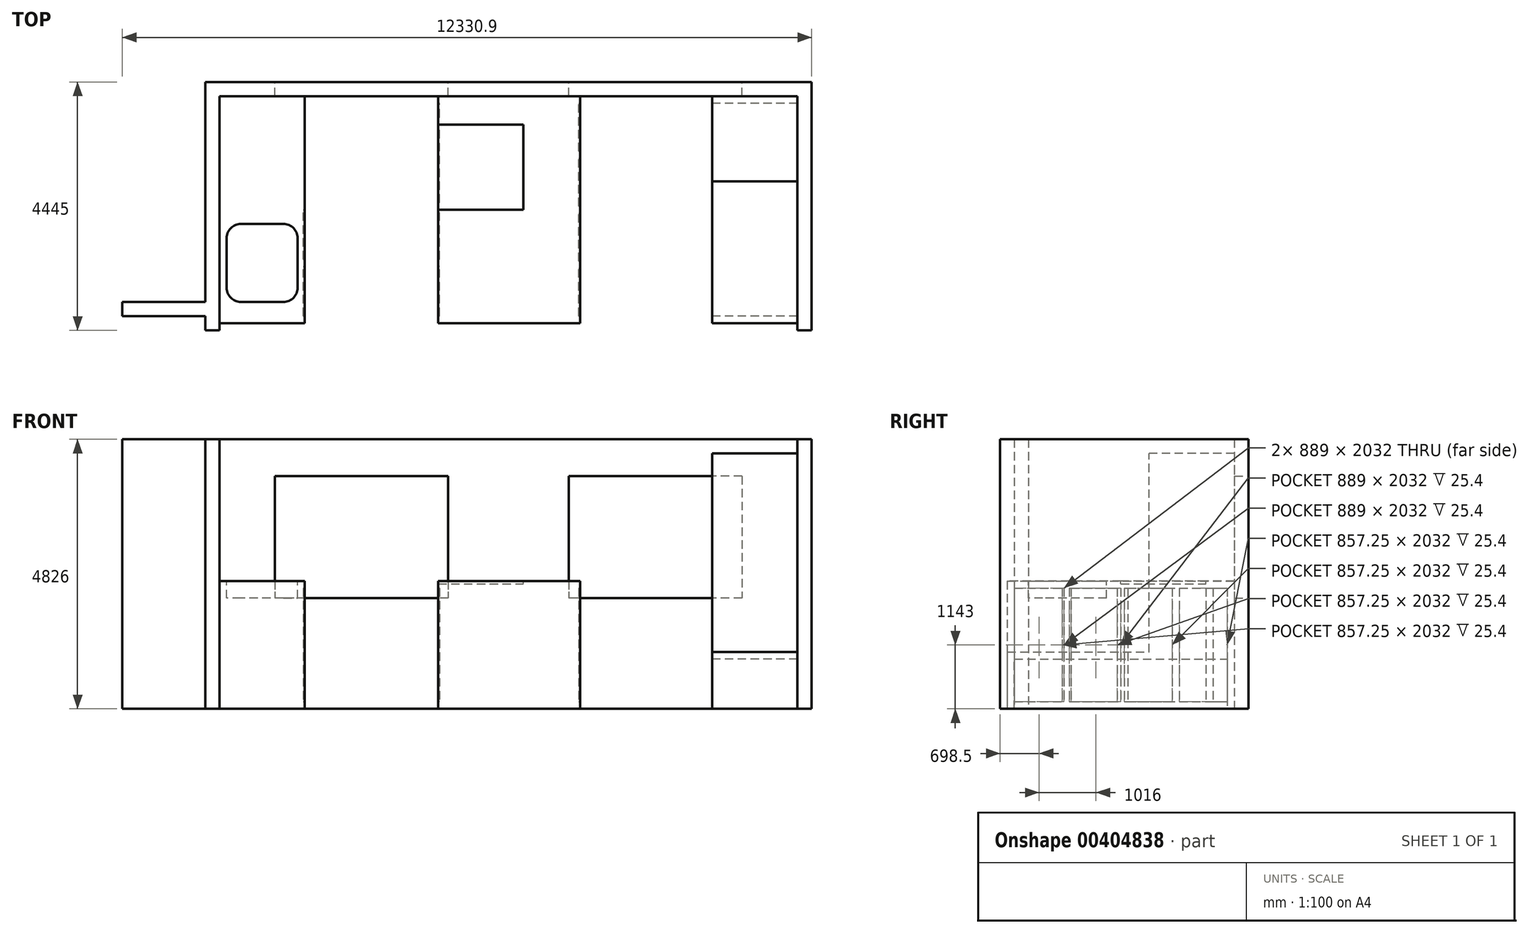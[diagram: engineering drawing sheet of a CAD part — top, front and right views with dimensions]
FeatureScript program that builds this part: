
annotation { "Feature Type Name" : "Feature", "Feature Type Description" : "" }
export const myFeature = defineFeature(function(context is Context, id is Id, definition is map)
    precondition{}
    {
        {
            var Q0;
            Q0=qCreatedBy(makeId("Top.planeOp"),FACE);
            var sketch = newSketch(context, id + "F0", { "sketchPlane" : qUnion([Q0])});
            skLineSegment(sketch, "E0", {"start": v(0, 0) * mm, "end": v(254, 0) * mm});
            skLineSegment(sketch, "E1", {"start": v(254, 0) * mm, "end": v(254, 4445) * mm});
            skLineSegment(sketch, "E2", {"start": v(254, 4445) * mm, "end": v(-10591.8, 4445) * mm});
            skLineSegment(sketch, "E3", {"start": v(-10591.8, 4445) * mm, "end": v(-10591.8, 508) * mm});
            skLineSegment(sketch, "E4", {"start": v(-10591.8, 508) * mm, "end": v(-12076.86, 508) * mm});
            skLineSegment(sketch, "E5", {"start": v(-12076.86, 508) * mm, "end": v(-12076.86, 254) * mm});
            skLineSegment(sketch, "E6", {"start": v(-12076.86, 254) * mm, "end": v(-10591.8, 254) * mm});
            skLineSegment(sketch, "E7", {"start": v(-10591.8, 254) * mm, "end": v(-10591.8, 0) * mm});
            skLineSegment(sketch, "E8", {"start": v(-10591.8, 0) * mm, "end": v(-10337.8, 0) * mm});
            skLineSegment(sketch, "E9", {"start": v(-10337.8, 0) * mm, "end": v(-10337.8, 4191) * mm});
            skLineSegment(sketch, "E10", {"start": v(-10337.8, 4191) * mm, "end": v(0, 4191) * mm});
            skLineSegment(sketch, "E11", {"start": v(0, 4191) * mm, "end": v(0, 0) * mm});
            skLineSegment(sketch, "E12", {"start": v(254, -2032) * mm, "end": v(0, -2032) * mm});
            skLineSegment(sketch, "E13", {"start": v(0, -2032) * mm, "end": v(0, -2286) * mm});
            skLineSegment(sketch, "E14", {"start": v(0, -2286) * mm, "end": v(-8051.8, -2286) * mm});
            skLineSegment(sketch, "E15", {"start": v(-10337.8, -2286) * mm, "end": v(-10337.8, -2032) * mm});
            skLineSegment(sketch, "E16", {"start": v(-10337.8, -2032) * mm, "end": v(-10591.8, -2032) * mm});
            skLineSegment(sketch, "E17", {"start": v(-10591.8, -2032) * mm, "end": v(-10591.8, -2286) * mm});
            skLineSegment(sketch, "E18", {"start": v(-10591.8, -2286) * mm, "end": v(-12107.08, -2286) * mm});
            skLineSegment(sketch, "E19", {"start": v(-12107.08, -2286) * mm, "end": v(-12107.08, -2540) * mm});
            skLineSegment(sketch, "E20", {"start": v(-12107.08, -2540) * mm, "end": v(-10591.8, -2540) * mm});
            skLineSegment(sketch, "E21", {"start": v(-10591.8, -2540) * mm, "end": v(-10591.8, -2794) * mm});
            skLineSegment(sketch, "E22", {"start": v(-10591.8, -2794) * mm, "end": v(-10337.8, -2794) * mm});
            skLineSegment(sketch, "E23", {"start": v(-10337.8, -2794) * mm, "end": v(-10337.8, -2540) * mm});
            skLineSegment(sketch, "E24", {"start": v(-10337.8, -2540) * mm, "end": v(-10083.8, -2540) * mm});
            skLineSegment(sketch, "E25", {"start": v(-10083.8, -2540) * mm, "end": v(-10083.8, -2286) * mm});
            skLineSegment(sketch, "E26", {"start": v(-8051.8, -2286) * mm, "end": v(-8051.8, -2540) * mm});
            skLineSegment(sketch, "E27", {"start": v(-8051.8, -2540) * mm, "end": v(0, -2540) * mm});
            skLineSegment(sketch, "E28", {"start": v(0, -2540) * mm, "end": v(0, -2794) * mm});
            skLineSegment(sketch, "E29", {"start": v(0, -2794) * mm, "end": v(254, -2794) * mm});
            skLineSegment(sketch, "E30", {"start": v(254, -2794) * mm, "end": v(254, -2540) * mm});
            skLineSegment(sketch, "E31", {"start": v(254, -2540) * mm, "end": v(508, -2540) * mm});
            skLineSegment(sketch, "E32", {"start": v(508, -2540) * mm, "end": v(508, -2286) * mm});
            skLineSegment(sketch, "E33", {"start": v(508, -2286) * mm, "end": v(254, -2286) * mm});
            skLineSegment(sketch, "E34", {"start": v(254, -2286) * mm, "end": v(254, -2032) * mm});
            skLineSegment(sketch, "E35.trimOffspring", {"start": v(-10083.8, -2286) * mm, "end": v(-10337.8, -2286) * mm});
            skLineSegment(sketch, "E36", {"start": v(-8813.8, 4191) * mm, "end": v(-8813.8, 127) * mm});
            skLineSegment(sketch, "E37", {"start": v(-8813.8, 127) * mm, "end": v(-10337.8, 127) * mm});
            skLineSegment(sketch, "E38", {"start": v(-6426.2, 4191) * mm, "end": v(-6426.2, 127) * mm});
            skLineSegment(sketch, "E39", {"start": v(-6426.2, 127) * mm, "end": v(-3886.2, 127) * mm});
            skLineSegment(sketch, "E40", {"start": v(-3886.2, 127) * mm, "end": v(-3886.2, 4191) * mm});
            skLineSegment(sketch, "E41", {"start": v(-6426.2, 3683) * mm, "end": v(-4902.2, 3683) * mm});
            skLineSegment(sketch, "E42", {"start": v(-4902.2, 3683) * mm, "end": v(-4902.2, 2159) * mm});
            skLineSegment(sketch, "E43", {"start": v(-4902.2, 2159) * mm, "end": v(-6426.2, 2159) * mm});
            skLineSegment(sketch, "E44", {"start": v(-1524, 4191) * mm, "end": v(-1524, 2667) * mm});
            skLineSegment(sketch, "E45", {"start": v(-1524, 2667) * mm, "end": v(0, 2667) * mm});
            skLineSegment(sketch, "E46", {"start": v(-1524, 2667) * mm, "end": v(-1524, 127) * mm});
            skLineSegment(sketch, "E47", {"start": v(-1524, 127) * mm, "end": v(0, 127) * mm});
            skLineSegment(sketch, "E48", {"start": v(-10337.8, 4191) * mm, "end": v(-8813.8, 4191) * mm});
            skLineSegment(sketch, "E49", {"start": v(-6426.2, 4191) * mm, "end": v(-3886.2, 4191) * mm});
            skLineSegment(sketch, "E50", {"start": v(-1524, 4191) * mm, "end": v(0, 4191) * mm});
            skSolve(sketch);
        }
        {
            var Q0;
            {var subQ0=sQuery(id+"F0.wireOp",EDGE,"E0");Q0=makeQuery(id+"F0.imprint","IMPRINT",FACE,{"disambiguationData":[TD([[makeQuery(id+"F0.imprint","IMPRINT",EDGE,{"derivedFrom":subQ0}),1.0]])]});}
            extrude(context, id + "F1", {"entities" : qUnion([Q0]), "depth" : 4826 * mm});
        }
        {
            var Q0;
            Q0=makeQuery(id+"F1.opExtrude","SWEPT_FACE",FACE,{"disambiguationData":[OSD([sQuery(id+"F0.wireOp",EDGE,"E2")])]});
            var sketch = newSketch(context, id + "F2", { "sketchPlane" : qUnion([Q0])});
            skLineSegment(sketch, "E51.bottom", {"start": v(990.6, 4165.6) * mm, "end": v(4089.4, 4165.6) * mm});
            skLineSegment(sketch, "E51.top", {"start": v(990.6, 1981.2) * mm, "end": v(4089.4, 1981.2) * mm});
            skLineSegment(sketch, "E51.left", {"start": v(990.6, 4165.6) * mm, "end": v(990.6, 1981.2) * mm});
            skLineSegment(sketch, "E51.right", {"start": v(4089.4, 4165.6) * mm, "end": v(4089.4, 1981.2) * mm});
            skLineSegment(sketch, "E52.bottom", {"start": v(6248.4, 4165.6) * mm, "end": v(9347.2, 4165.6) * mm});
            skLineSegment(sketch, "E52.top", {"start": v(6248.4, 1981.2) * mm, "end": v(9347.2, 1981.2) * mm});
            skLineSegment(sketch, "E52.left", {"start": v(6248.4, 4165.6) * mm, "end": v(6248.4, 1981.2) * mm});
            skLineSegment(sketch, "E52.right", {"start": v(9347.2, 4165.6) * mm, "end": v(9347.2, 1981.2) * mm});
            skSolve(sketch);
        }
        {
            var Q0;
            Q0=qSketchRegion(id+"F2",true);
            extrude(context, id + "F3", {"entities" : qUnion([Q0]), "operationType" : NewBodyOperationType.REMOVE, "oppositeDirection" : true, "depth" : 254 * mm});
        }
        {
            var Q0;
            Q0=makeQuery(id+"F0.imprint","IMPRINT",FACE,{"disambiguationData":[TD([[makeQuery(id+"F0.imprint","IMPRINT",EDGE,{"derivedFrom":sQuery(id+"F0.wireOp",EDGE,"E36")}),-1.0]])]});
            var Q1;
            {var subQ0=sQuery(id+"F0.wireOp",EDGE,"E41");Q1=makeQuery(id+"F0.imprint","IMPRINT",FACE,{"disambiguationData":[TD([[makeQuery(id+"F0.imprint","IMPRINT",EDGE,{"derivedFrom":subQ0}),-1.0]])]});}
            var Q2;
            {var subQ0=sQuery(id+"F0.wireOp",EDGE,"E39");Q2=makeQuery(id+"F0.imprint","IMPRINT",FACE,{"disambiguationData":[TD([[makeQuery(id+"F0.imprint","IMPRINT",EDGE,{"derivedFrom":subQ0}),1.0]])]});}
            extrude(context, id + "F4", {"entities" : qUnion([Q0, Q1, Q2]), "operationType" : NewBodyOperationType.ADD, "depth" : 2286 * mm});
        }
        {
            var Q0;
            {var subQ0=sQuery(id+"F0.wireOp",EDGE,"E45");Q0=makeQuery(id+"F0.imprint","IMPRINT",FACE,{"disambiguationData":[TD([[makeQuery(id+"F0.imprint","IMPRINT",EDGE,{"derivedFrom":subQ0}),-1.0]])]});}
            var Q1;
            {var subQ3=sQuery(id+"F0.wireOp",EDGE,"E44");Q1=makeQuery(id+"F0.imprint","IMPRINT",FACE,{"disambiguationData":[TD([[makeQuery(id+"F0.imprint","IMPRINT",EDGE,{"derivedFrom":subQ3}),1.0]])]});}
            extrude(context, id + "F5", {"entities" : qUnion([Q0, Q1]), "operationType" : NewBodyOperationType.ADD, "depth" : 4572 * mm});
        }
        {
            var Q0;
            Q0=makeQuery(id+"F5.opExtrude","SWEPT_FACE",FACE,{"disambiguationData":[OSD([sQuery(id+"F0.wireOp",EDGE,"E44"),sQuery(id+"F0.wireOp",EDGE,"E46")])]});
            var sketch = newSketch(context, id + "F6", { "sketchPlane" : qUnion([Q0])});
            skLineSegment(sketch, "E53", {"start": v(-254, 0) * mm, "end": v(-254, 889) * mm});
            skLineSegment(sketch, "E54", {"start": v(-254, 889) * mm, "end": v(-4064, 889) * mm});
            skLineSegment(sketch, "E55", {"start": v(-4064, 889) * mm, "end": v(-4064, 0) * mm});
            skLineSegment(sketch, "E56", {"start": v(-127, 1016) * mm, "end": v(-2667, 1016) * mm});
            skLineSegment(sketch, "E57", {"start": v(-2667, 1016) * mm, "end": v(-2667, 4572) * mm});
            skLineSegment(sketch, "E58", {"start": v(-2667, 1016) * mm, "end": v(-4191, 1016) * mm});
            skSolve(sketch);
        }
        {
            var Q0;
            Q0 = qSketchRegion(id + "F6", true);
            var Q1;
            {var subQ0=sQuery(id+"F6.wireOp",EDGE,"E56");Q1=makeQuery(id+"F6.imprint","IMPRINT",FACE,{"disambiguationData":[TD([[makeQuery(id+"F6.imprint","IMPRINT",EDGE,{"derivedFrom":subQ0}),-1.0]])]});}
            var Q2;
            {var subQ0=sQuery(id+"F6.wireOp",EDGE,"E53");Q2=makeQuery(id+"F6.imprint","IMPRINT",FACE,{"disambiguationData":[TD([[makeQuery(id+"F6.imprint","IMPRINT",EDGE,{"derivedFrom":subQ0}),1.0]])]});}
            extrude(context, id + "F7", {"entities" : qUnion([Q0, Q1, Q2]), "operationType" : NewBodyOperationType.REMOVE, "oppositeDirection" : true, "depth" : 1524 * mm});
        }
        {
            var Q0;
            Q0=makeQuery(id+"F4.opExtrude","CAP_FACE",FACE,{"disambiguationData":[OSD([sQuery(id+"F0.wireOp",EDGE,"E0"),sQuery(id+"F0.wireOp",EDGE,"E1"),sQuery(id+"F0.wireOp",EDGE,"E2"),sQuery(id+"F0.wireOp",EDGE,"E3"),sQuery(id+"F0.wireOp",EDGE,"E4"),sQuery(id+"F0.wireOp",EDGE,"E5"),sQuery(id+"F0.wireOp",EDGE,"E6"),sQuery(id+"F0.wireOp",EDGE,"E7"),sQuery(id+"F0.wireOp",EDGE,"E8"),sQuery(id+"F0.wireOp",EDGE,"E9"),sQuery(id+"F0.wireOp",EDGE,"E10"),sQuery(id+"F0.wireOp",EDGE,"E11"),sQuery(id+"F0.wireOp",EDGE,"E36"),sQuery(id+"F0.wireOp",EDGE,"E37"),sQuery(id+"F0.wireOp",EDGE,"E38"),sQuery(id+"F0.wireOp",EDGE,"E39"),sQuery(id+"F0.wireOp",EDGE,"E40")])],"isStart":false});
            var sketch = newSketch(context, id + "F8", { "sketchPlane" : qUnion([Q0])});
            skLineSegment(sketch, "E59", {"start": v(-6426.2, 3683) * mm, "end": v(-4902.2, 3683) * mm});
            skLineSegment(sketch, "E60", {"start": v(-4902.2, 3683) * mm, "end": v(-4902.2, 2159) * mm});
            skLineSegment(sketch, "E61", {"start": v(-4902.2, 2159) * mm, "end": v(-6426.2, 2159) * mm});
            skLineSegment(sketch, "E62", {"start": v(-6426.2, 2159) * mm, "end": v(-6426.2, 3683) * mm});
            skSolve(sketch);
        }
        {
            var Q0;
            Q0 = qSketchRegion(id + "F8", true);
            extrude(context, id + "F9", {"entities" : qUnion([Q0]), "operationType" : NewBodyOperationType.REMOVE, "oppositeDirection" : true, "depth" : 50.8 * mm});
        }
        {
            var Q0;
            Q0=makeQuery(id+"F4.opExtrude","CAP_FACE",FACE,{"disambiguationData":[OSD([sQuery(id+"F0.wireOp",EDGE,"E0"),sQuery(id+"F0.wireOp",EDGE,"E1"),sQuery(id+"F0.wireOp",EDGE,"E2"),sQuery(id+"F0.wireOp",EDGE,"E3"),sQuery(id+"F0.wireOp",EDGE,"E4"),sQuery(id+"F0.wireOp",EDGE,"E5"),sQuery(id+"F0.wireOp",EDGE,"E6"),sQuery(id+"F0.wireOp",EDGE,"E7"),sQuery(id+"F0.wireOp",EDGE,"E8"),sQuery(id+"F0.wireOp",EDGE,"E9"),sQuery(id+"F0.wireOp",EDGE,"E10"),sQuery(id+"F0.wireOp",EDGE,"E11"),sQuery(id+"F0.wireOp",EDGE,"E36"),sQuery(id+"F0.wireOp",EDGE,"E37"),sQuery(id+"F0.wireOp",EDGE,"E38"),sQuery(id+"F0.wireOp",EDGE,"E39"),sQuery(id+"F0.wireOp",EDGE,"E40")])],"isStart":false});
            var sketch = newSketch(context, id + "F10", { "sketchPlane" : qUnion([Q0])});
            skLineSegment(sketch, "E63", {"start": v(-9194.8, 1905) * mm, "end": v(-9956.8, 1905) * mm});
            skLineSegment(sketch, "E64", {"start": v(-10210.8, 1651) * mm, "end": v(-10210.8, 762) * mm});
            skLineSegment(sketch, "E65", {"start": v(-9956.8, 508) * mm, "end": v(-9194.8, 508) * mm});
            skLineSegment(sketch, "E66", {"start": v(-8940.8, 762) * mm, "end": v(-8940.8, 1651) * mm});
            skPoint(sketch, "E67.visualSharp", {"position": v(-8940.8, 1905) * mm});
            skArc(sketch, "E67.filletArc", {"start": v(-8940.8, 1651) * mm, "mid": v(-9015.2, 1830.6) * mm, "end": v(-9194.8, 1905) * mm});
            skPoint(sketch, "E68.visualSharp", {"position": v(-10210.8, 1905) * mm});
            skArc(sketch, "E68.filletArc", {"start": v(-9956.8, 1905) * mm, "mid": v(-10136.4, 1830.6) * mm, "end": v(-10210.8, 1651) * mm});
            skPoint(sketch, "E69.visualSharp", {"position": v(-10210.8, 508) * mm});
            skArc(sketch, "E69.filletArc", {"start": v(-10210.8, 762) * mm, "mid": v(-10136.4, 582.4) * mm, "end": v(-9956.8, 508) * mm});
            skPoint(sketch, "E70.visualSharp", {"position": v(-8940.8, 508) * mm});
            skArc(sketch, "E70.filletArc", {"start": v(-9194.8, 508) * mm, "mid": v(-9015.2, 582.4) * mm, "end": v(-8940.8, 762) * mm});
            skSolve(sketch);
        }
        {
            var Q0;
            Q0 = qSketchRegion(id + "F10", true);
            extrude(context, id + "F11", {"entities" : qUnion([Q0]), "operationType" : NewBodyOperationType.REMOVE, "oppositeDirection" : true, "depth" : 304.8 * mm});
        }
        {
            var Q0;
            Q0=makeQuery(id+"F4.opExtrude","SWEPT_FACE",FACE,{"disambiguationData":[OSD([sQuery(id+"F0.wireOp",EDGE,"E36")])]});
            var sketch = newSketch(context, id + "F12", { "sketchPlane" : qUnion([Q0])});
            skLineSegment(sketch, "E71.bottom", {"start": v(254, 2159) * mm, "end": v(1143, 2159) * mm});
            skLineSegment(sketch, "E71.top", {"start": v(254, 127) * mm, "end": v(1143, 127) * mm});
            skLineSegment(sketch, "E71.left", {"start": v(254, 2159) * mm, "end": v(254, 127) * mm});
            skLineSegment(sketch, "E71.right", {"start": v(1143, 2159) * mm, "end": v(1143, 127) * mm});
            skLineSegment(sketch, "E72.bottom", {"start": v(1270, 2159) * mm, "end": v(2159, 2159) * mm});
            skLineSegment(sketch, "E72.top", {"start": v(1270, 127) * mm, "end": v(2159, 127) * mm});
            skLineSegment(sketch, "E72.left", {"start": v(1270, 2159) * mm, "end": v(1270, 127) * mm});
            skLineSegment(sketch, "E72.right", {"start": v(2159, 2159) * mm, "end": v(2159, 127) * mm});
            skSolve(sketch);
        }
        {
            var Q0;
            Q0 = qSketchRegion(id + "F12", true);
            extrude(context, id + "F13", {"entities" : qUnion([Q0]), "operationType" : NewBodyOperationType.REMOVE, "oppositeDirection" : true, "depth" : 25.4 * mm});
        }
        {
            var Q0;
            Q0=makeQuery(id+"F4.opExtrude","SWEPT_FACE",FACE,{"disambiguationData":[OSD([sQuery(id+"F0.wireOp",EDGE,"E40")])]});
            var sketch = newSketch(context, id + "F14", { "sketchPlane" : qUnion([Q0])});
            skLineSegment(sketch, "E73.bottom", {"start": v(254, 2159) * mm, "end": v(1111.25, 2159) * mm});
            skLineSegment(sketch, "E73.top", {"start": v(254, 127) * mm, "end": v(1111.25, 127) * mm});
            skLineSegment(sketch, "E73.left", {"start": v(254, 2159) * mm, "end": v(254, 127) * mm});
            skLineSegment(sketch, "E73.right", {"start": v(1111.25, 2159) * mm, "end": v(1111.25, 127) * mm});
            skLineSegment(sketch, "E74.bottom", {"start": v(1238.25, 2159) * mm, "end": v(2095.5, 2159) * mm});
            skLineSegment(sketch, "E74.top", {"start": v(1238.25, 127) * mm, "end": v(2095.5, 127) * mm});
            skLineSegment(sketch, "E74.left", {"start": v(1238.25, 2159) * mm, "end": v(1238.25, 127) * mm});
            skLineSegment(sketch, "E74.right", {"start": v(2095.5, 2159) * mm, "end": v(2095.5, 127) * mm});
            skLineSegment(sketch, "E75.bottom", {"start": v(2222.5, 2159) * mm, "end": v(3079.75, 2159) * mm});
            skLineSegment(sketch, "E75.top", {"start": v(2222.5, 127) * mm, "end": v(3079.75, 127) * mm});
            skLineSegment(sketch, "E75.left", {"start": v(2222.5, 2159) * mm, "end": v(2222.5, 127) * mm});
            skLineSegment(sketch, "E75.right", {"start": v(3079.75, 2159) * mm, "end": v(3079.75, 127) * mm});
            skLineSegment(sketch, "E76.bottom", {"start": v(3206.75, 2159) * mm, "end": v(4064, 2159) * mm});
            skLineSegment(sketch, "E76.top", {"start": v(3206.75, 127) * mm, "end": v(4064, 127) * mm});
            skLineSegment(sketch, "E76.left", {"start": v(3206.75, 2159) * mm, "end": v(3206.75, 127) * mm});
            skLineSegment(sketch, "E76.right", {"start": v(4064, 2159) * mm, "end": v(4064, 127) * mm});
            skSolve(sketch);
        }
        {
            var Q0;
            Q0 = qSketchRegion(id + "F14", true);
            extrude(context, id + "F15", {"entities" : qUnion([Q0]), "operationType" : NewBodyOperationType.REMOVE, "oppositeDirection" : true, "depth" : 25.4 * mm});
        }
        {
            var Q0;
            Q0=makeQuery(id+"F4.opExtrude","SWEPT_FACE",FACE,{"disambiguationData":[OSD([sQuery(id+"F0.wireOp",EDGE,"E38")])]});
            var sketch = newSketch(context, id + "F16", { "sketchPlane" : qUnion([Q0])});
            skLineSegment(sketch, "E77.bottom", {"start": v(-254, 2159) * mm, "end": v(-1143, 2159) * mm});
            skLineSegment(sketch, "E77.top", {"start": v(-254, 127) * mm, "end": v(-1143, 127) * mm});
            skLineSegment(sketch, "E77.left", {"start": v(-254, 2159) * mm, "end": v(-254, 127) * mm});
            skLineSegment(sketch, "E77.right", {"start": v(-1143, 2159) * mm, "end": v(-1143, 127) * mm});
            skLineSegment(sketch, "E78.bottom", {"start": v(-1270, 2159) * mm, "end": v(-2159, 2159) * mm});
            skLineSegment(sketch, "E78.top", {"start": v(-1270, 127) * mm, "end": v(-2159, 127) * mm});
            skLineSegment(sketch, "E78.left", {"start": v(-1270, 2159) * mm, "end": v(-1270, 127) * mm});
            skLineSegment(sketch, "E78.right", {"start": v(-2159, 2159) * mm, "end": v(-2159, 127) * mm});
            skLineSegment(sketch, "E79.bottom", {"start": v(-2286, 2159) * mm, "end": v(-3683, 2159) * mm});
            skLineSegment(sketch, "E79.top", {"start": v(-2286, 127) * mm, "end": v(-3683, 127) * mm});
            skLineSegment(sketch, "E79.left", {"start": v(-2286, 2159) * mm, "end": v(-2286, 127) * mm});
            skLineSegment(sketch, "E79.right", {"start": v(-3683, 2159) * mm, "end": v(-3683, 127) * mm});
            skLineSegment(sketch, "E80.bottom", {"start": v(-3810, 2159) * mm, "end": v(-4064, 2159) * mm});
            skLineSegment(sketch, "E80.top", {"start": v(-3810, 127) * mm, "end": v(-4064, 127) * mm});
            skLineSegment(sketch, "E80.left", {"start": v(-3810, 2159) * mm, "end": v(-3810, 127) * mm});
            skLineSegment(sketch, "E80.right", {"start": v(-4064, 2159) * mm, "end": v(-4064, 127) * mm});
            skSolve(sketch);
        }
        {
            var Q0;
            Q0 = qSketchRegion(id + "F16", true);
            extrude(context, id + "F17", {"entities" : qUnion([Q0]), "operationType" : NewBodyOperationType.REMOVE, "oppositeDirection" : true, "depth" : 25.4 * mm});
        }
    });
